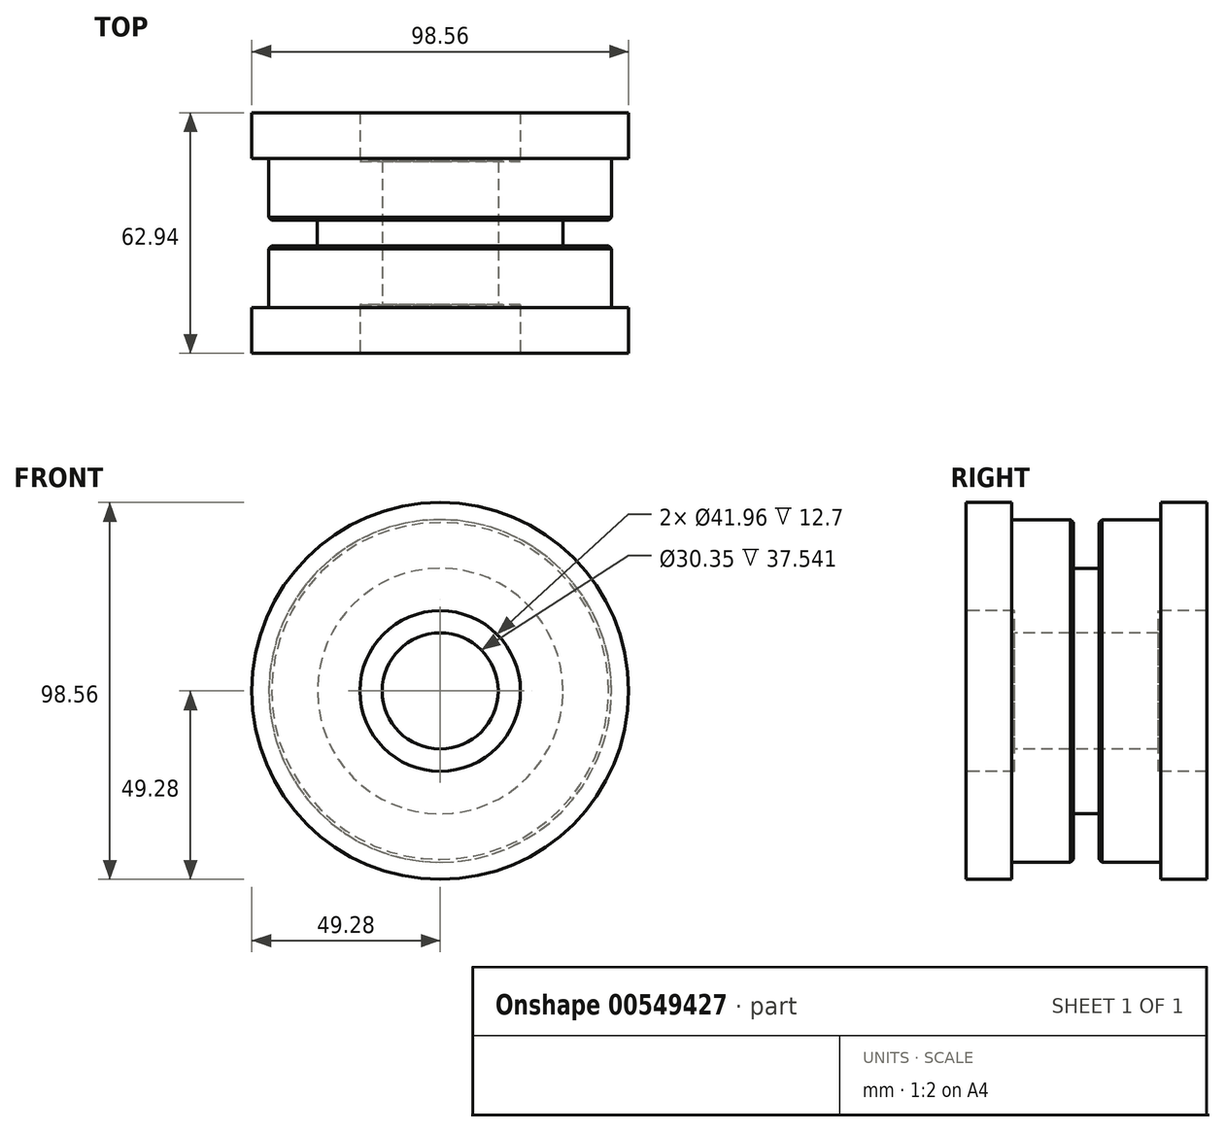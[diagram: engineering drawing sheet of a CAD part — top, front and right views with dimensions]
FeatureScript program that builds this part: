
annotation { "Feature Type Name" : "Feature", "Feature Type Description" : "" }
export const myFeature = defineFeature(function(context is Context, id is Id, definition is map)
    precondition{}
    {
        {
            var Q0;
            Q0=qCreatedBy(makeId("Right.planeOp"),FACE);
            var sketch = newSketch(context, id + "F0", { "sketchPlane" : qUnion([Q0])});
            skLineSegment(sketch, "E0", {"start": v(-35.21, 0) * mm, "end": v(33.24, 0) * mm, "construction": true});
            skLineSegment(sketch, "E1", {"start": v(0, 15.18) * mm, "end": v(-18.77, 15.18) * mm});
            skLineSegment(sketch, "E2", {"start": v(-18.77, 15.18) * mm, "end": v(-18.77, 20.98) * mm});
            skLineSegment(sketch, "E3", {"start": v(-18.77, 20.98) * mm, "end": v(-31.47, 20.98) * mm});
            skLineSegment(sketch, "E4", {"start": v(-31.47, 20.98) * mm, "end": v(-31.47, 49.28) * mm});
            skLineSegment(sketch, "E5", {"start": v(-31.47, 49.28) * mm, "end": v(-19.5, 49.28) * mm});
            skLineSegment(sketch, "E6", {"start": v(-19.5, 49.28) * mm, "end": v(-19.5, 44.8) * mm});
            skLineSegment(sketch, "E7", {"start": v(-19.5, 44.8) * mm, "end": v(-3.37, 44.8) * mm});
            skLineSegment(sketch, "E8", {"start": v(0, 44.8) * mm, "end": v(0, 15.18) * mm, "construction": true});
            skLineSegment(sketch, "E9.MirrorCS", {"start": v(19.5, 44.8) * mm, "end": v(3.37, 44.8) * mm});
            skLineSegment(sketch, "E10.MirrorCS", {"start": v(19.5, 49.28) * mm, "end": v(19.5, 44.8) * mm});
            skLineSegment(sketch, "E11.MirrorCS", {"start": v(31.47, 49.28) * mm, "end": v(19.5, 49.28) * mm});
            skLineSegment(sketch, "E12.MirrorCS", {"start": v(31.47, 20.98) * mm, "end": v(31.47, 49.28) * mm});
            skLineSegment(sketch, "E13.MirrorCS", {"start": v(18.77, 20.98) * mm, "end": v(31.47, 20.98) * mm});
            skLineSegment(sketch, "E14.MirrorCS", {"start": v(18.77, 15.18) * mm, "end": v(18.77, 20.98) * mm});
            skLineSegment(sketch, "E15.MirrorCS", {"start": v(0, 15.18) * mm, "end": v(18.77, 15.18) * mm});
            skLineSegment(sketch, "E16", {"start": v(-3.37, 44.8) * mm, "end": v(-3.37, 32.1) * mm});
            skLineSegment(sketch, "E17", {"start": v(-3.37, 32.1) * mm, "end": v(3.37, 32.1) * mm});
            skLineSegment(sketch, "E18", {"start": v(3.37, 32.1) * mm, "end": v(3.37, 44.8) * mm});
            skPoint(sketch, "E19.orphan", {"position": v(0, 44.8) * mm});
            skSolve(sketch);
        }
        {
            var Q0;
            Q0=qSketchRegion(id+"F0",true);
            var Q1;
            Q1=sQuery(id+"F0.wireOp",EDGE,"E0");
            revolve(context, id + "F1", {"entities" : qUnion([Q0]), "axis" : qUnion([Q1]), "revolveType" : RevolveType.FULL});
        }
        {
            var Q0;
            Q0=makeQuery(id+"F1.opRevolve","SWEPT_EDGE",EDGE,{"disambiguationData":[OSD([sQuery(id+"F0.wireOp",EDGE,"E9.MirrorCS"),sQuery(id+"F0.wireOp",EDGE,"E18")])]});
            var Q1;
            Q1=makeQuery(id+"F1.opRevolve","SWEPT_EDGE",EDGE,{"disambiguationData":[OSD([sQuery(id+"F0.wireOp",EDGE,"E7"),sQuery(id+"F0.wireOp",EDGE,"E16")])]});
            chamfer(context, id + "F2", {"entities" : qUnion([Q0, Q1]), "width" : 0.76 * mm, "tangentPropagation" : true});
        }
    });
